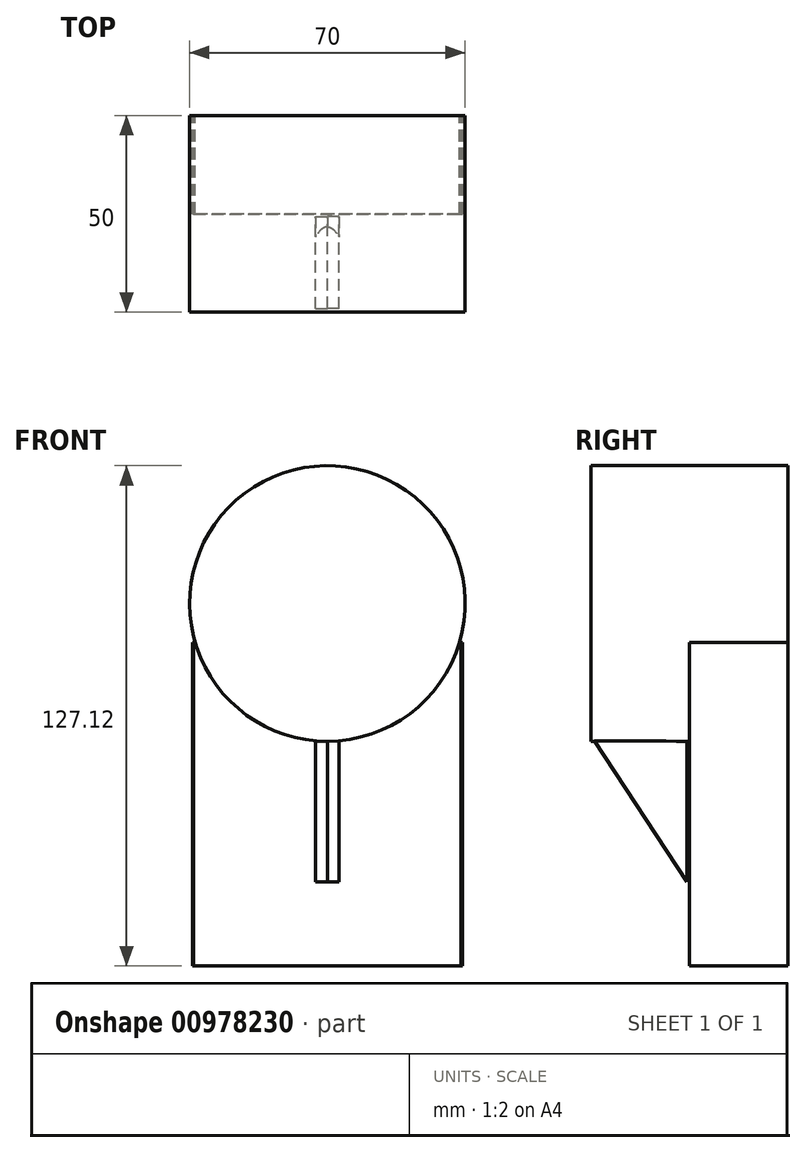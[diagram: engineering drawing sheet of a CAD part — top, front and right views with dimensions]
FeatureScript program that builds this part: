
annotation { "Feature Type Name" : "Feature", "Feature Type Description" : "" }
export const myFeature = defineFeature(function(context is Context, id is Id, definition is map)
    precondition{}
    {
        {
            var Q0;
            Q0=qCreatedBy(makeId("Front.planeOp"),FACE);
            var sketch = newSketch(context, id + "F0", { "sketchPlane" : qUnion([Q0])});
            skCircle(sketch, "E0", {"center": v(0, 47.18) * mm, "radius": 35 * mm});
            skSolve(sketch);
        }
        {
            var Q0;
            Q0=makeQuery(id+"F0.imprint","IMPRINT",FACE,{"disambiguationData":[TD([[makeQuery(id+"F0.imprint","IMPRINT",EDGE,{"derivedFrom":sQuery(id+"F0.wireOp",EDGE,"E0")}),1.0]])]});
            extrude(context, id + "F1", {"entities" : qUnion([Q0]), "depth" : 50 * mm, "offsetDistance" : 25 * mm});
        }
        {
            var Q0;
            Q0=qCreatedBy(makeId("Front.planeOp"),FACE);
            var sketch = newSketch(context, id + "F2", { "sketchPlane" : qUnion([Q0])});
            skLineSegment(sketch, "E1.bottom", {"start": v(-33.99, 37.28) * mm, "end": v(34.28, 37.28) * mm});
            skLineSegment(sketch, "E1.top", {"start": v(-33.99, -44.94) * mm, "end": v(34.28, -44.94) * mm});
            skLineSegment(sketch, "E1.left", {"start": v(-33.99, 37.28) * mm, "end": v(-33.99, -44.94) * mm});
            skLineSegment(sketch, "E1.right", {"start": v(34.28, 37.28) * mm, "end": v(34.28, -44.94) * mm});
            skSolve(sketch);
        }
        {
            var Q0;
            Q0=makeQuery(id+"F2.imprint","IMPRINT",FACE,{"disambiguationData":[TD([[makeQuery(id+"F2.imprint","IMPRINT",EDGE,{"derivedFrom":sQuery(id+"F2.wireOp",EDGE,"E1.bottom")}),-1.0]])]});
            extrude(context, id + "F3", {"entities" : qUnion([Q0]), "operationType" : NewBodyOperationType.ADD, "depth" : 25 * mm, "offsetDistance" : 25 * mm});
        }
        {
            var Q0;
            Q0=qCreatedBy(makeId("Right.planeOp"),FACE);
            var sketch = newSketch(context, id + "F4", { "sketchPlane" : qUnion([Q0])});
            skLineSegment(sketch, "E2", {"start": v(-49.72, 13.24) * mm, "end": v(-25.68, -23.57) * mm});
            skLineSegment(sketch, "E3", {"start": v(-25.68, -23.57) * mm, "end": v(-25.68, 12.05) * mm});
            skLineSegment(sketch, "E4", {"start": v(-25.68, 12.05) * mm, "end": v(-49.72, 13.24) * mm});
            skSolve(sketch);
        }
        {
            var Q0;
            Q0=makeQuery(id+"F4.imprint","IMPRINT",FACE,{"disambiguationData":[TD([[makeQuery(id+"F4.imprint","IMPRINT",EDGE,{"derivedFrom":sQuery(id+"F4.wireOp",EDGE,"E2")}),1.0]])]});
            extrude(context, id + "F5", {"entities" : qUnion([Q0]), "operationType" : NewBodyOperationType.ADD, "depth" : 3 * mm, "offsetDistance" : 25 * mm});
        }
        {
            var Q0;
            Q0=makeQuery(id+"F1.opExtrude","SWEPT_BODY",BODY,{"disambiguationData":[OSD([sQuery(id+"F0.wireOp",EDGE,"E0")])]});
            var Q1;
            Q1=makeQuery(id+"F5.opExtrude","CAP_FACE",FACE,{"disambiguationData":[OSD([sQuery(id+"F4.wireOp",EDGE,"E2"),sQuery(id+"F4.wireOp",EDGE,"E3"),sQuery(id+"F4.wireOp",EDGE,"E4")])],"isStart":true});
            mirror(context, id + "F6", {"entities" : qUnion([Q0]), "mirrorPlane" : qUnion([Q1])});
        }
    });
